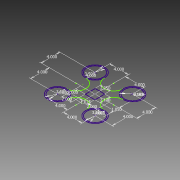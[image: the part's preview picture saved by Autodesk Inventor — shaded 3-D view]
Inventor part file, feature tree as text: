
AUTODESK INVENTOR PART (.ipt)
format: ipt  version: 2015 (Build 190159000, 159)  size: 86,528 bytes
history: native  units: in
note: dims shown in document units (in); Inventor stores cm internally (conversion verified against a paired STEP export)
features: sketch x1
ambient origin geometry x8: Origin, YZ Plane, XZ Plane, XY Plane, X Axis, Y Axis, Z Axis, Center Point
feature tree (1):
  sketch  "Sketch1"  dims[d0=2.05in d1=2.1in d4=4.0in d5=3.5in d12=4.0in d13=3.5in d14=4.0in d15=3.5in d16=4.0in d17=3.5in d19=2.0in d20=2.0in d21=2.0in d22=4.0in d23=4.0in d24=4.0in d25=4.0in d26=4.0in d27=4.0in d28=1.05in d29=1.025in d30=4.0in d31=4.0in]
